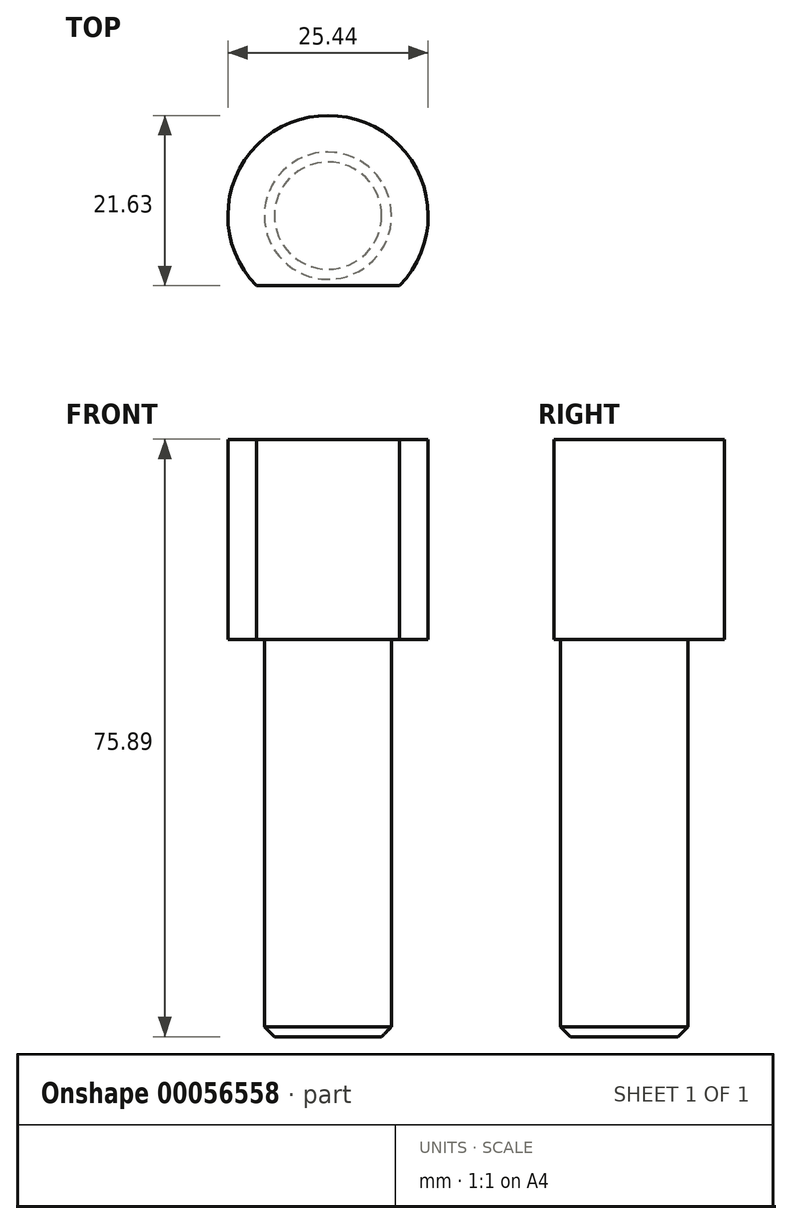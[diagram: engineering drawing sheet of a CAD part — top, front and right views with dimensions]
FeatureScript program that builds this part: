
annotation { "Feature Type Name" : "Feature", "Feature Type Description" : "" }
export const myFeature = defineFeature(function(context is Context, id is Id, definition is map)
    precondition{}
    {
        {
            var Q0;
            Q0=qCreatedBy(makeId("Top.planeOp"),FACE);
            var sketch = newSketch(context, id + "F0", { "sketchPlane" : qUnion([Q0])});
            skCircle(sketch, "E0", {"center": v(0, 0) * mm, "radius": 8.08 * mm});
            skSolve(sketch);
        }
        {
            var Q0;
            Q0 = qSketchRegion(id + "F0", true);
            extrude(context, id + "F1", {"entities" : qUnion([Q0]), "depth" : 50.5 * mm});
        }
        {
            var Q0;
            Q0=makeQuery(id+"F1.opExtrude","CAP_FACE",FACE,{"disambiguationData":[OSD([sQuery(id+"F0.wireOp",EDGE,"E0")])],"isStart":false});
            var sketch = newSketch(context, id + "F2", { "sketchPlane" : qUnion([Q0])});
            skCircle(sketch, "E1", {"center": v(0, 0) * mm, "radius": 12.72 * mm});
            skSolve(sketch);
        }
        {
            var Q0;
            Q0 = qSketchRegion(id + "F2", true);
            extrude(context, id + "F3", {"entities" : qUnion([Q0]), "operationType" : NewBodyOperationType.ADD, "depth" : 25.4 * mm});
        }
        {
            var Q0;
            Q0=makeQuery(id+"F3.opExtrude","CAP_FACE",FACE,{"disambiguationData":[OSD([sQuery(id+"F2.wireOp",EDGE,"E1")])],"isStart":false});
            var sketch = newSketch(context, id + "F4", { "sketchPlane" : qUnion([Q0])});
            skLineSegment(sketch, "E2", {"start": v(-9.08, -8.9) * mm, "end": v(9.08, -8.9) * mm});
            skPoint(sketch, "E3.center.orphan", {"position": v(0, 0) * mm});
            skSolve(sketch);
        }
        {
            var Q0;
            {var subQ0=sQuery(id+"F4.wireOp",EDGE,"E2");Q0=makeQuery(id+"F4.imprint","IMPRINT",FACE,{"disambiguationData":[TD([[makeQuery(id+"F4.imprint","IMPRINT",EDGE,{"derivedFrom":subQ0}),-1.0]])]});}
            extrude(context, id + "F5", {"entities" : qUnion([Q0]), "operationType" : NewBodyOperationType.REMOVE, "oppositeDirection" : true, "depth" : 25.4 * mm});
        }
        {
            var Q0;
            Q0=makeQuery(id+"F1.opExtrude","CAP_EDGE",EDGE,{"disambiguationData":[OSD([sQuery(id+"F0.wireOp",EDGE,"E0")])],"isStart":true});
            var Q1;
            Q1=makeQuery(id+"F1.opExtrude","CAP_EDGE",EDGE,{"disambiguationData":[OSD([sQuery(id+"F0.wireOp",EDGE,"E0")])],"isStart":false});
            chamfer(context, id + "F6", {"entities" : qUnion([Q0, Q1]), "width" : 1.27 * mm, "tangentPropagation" : true});
        }
    });
